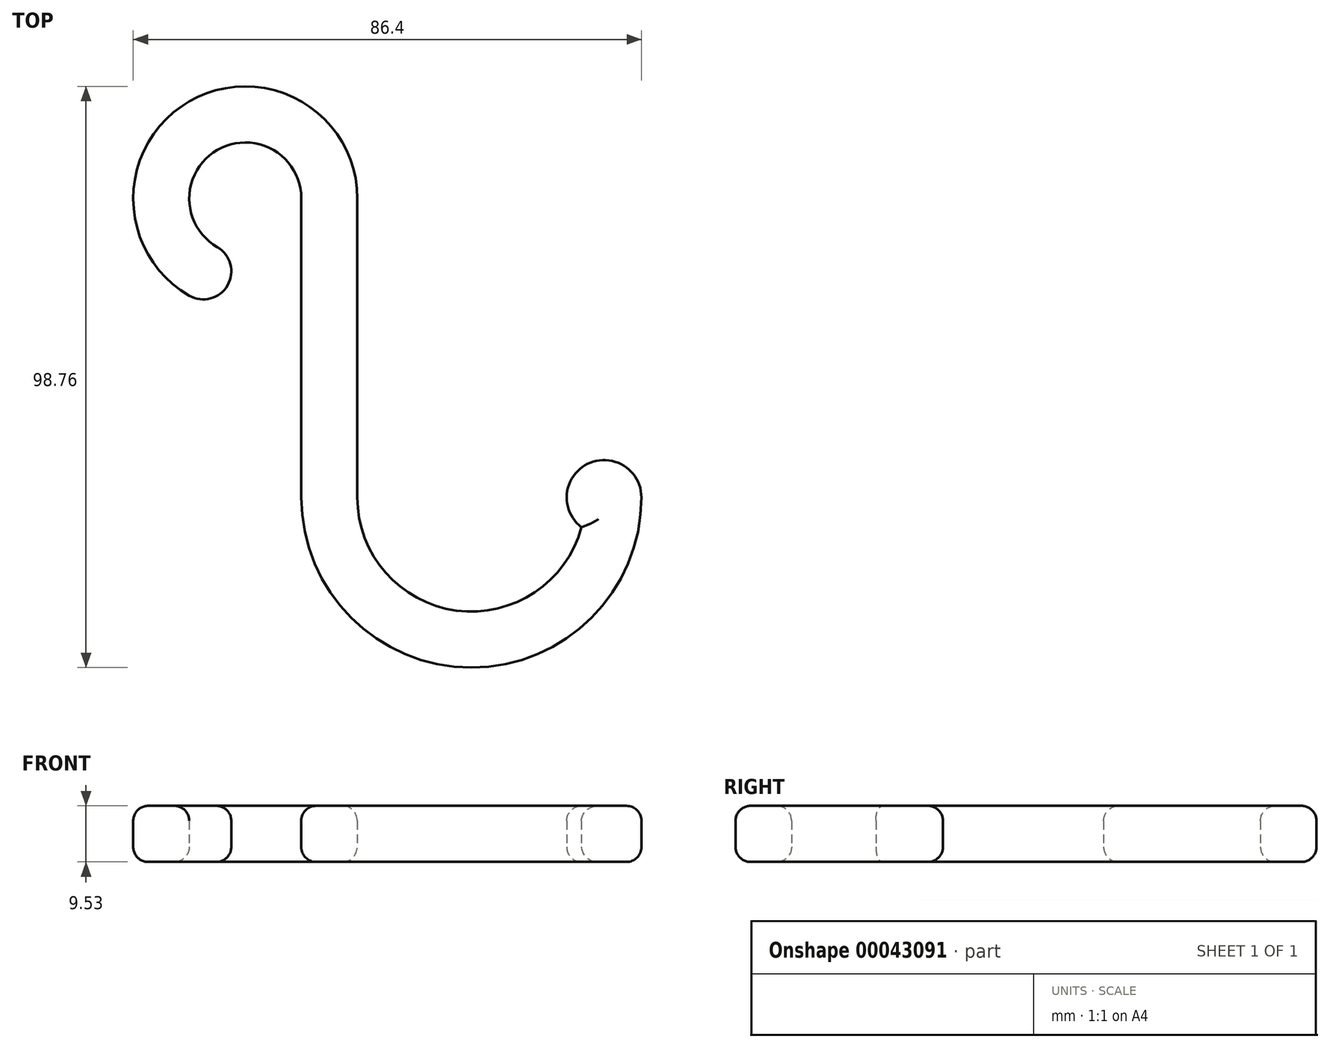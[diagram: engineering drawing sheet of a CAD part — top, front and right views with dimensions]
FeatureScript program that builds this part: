
annotation { "Feature Type Name" : "Feature", "Feature Type Description" : "" }
export const myFeature = defineFeature(function(context is Context, id is Id, definition is map)
    precondition{}
    {
        {
            var Q0;
            Q0=qCreatedBy(makeId("Top.planeOp"),FACE);
            var sketch = newSketch(context, id + "F0", { "sketchPlane" : qUnion([Q0])});
            skLineSegment(sketch, "E0.left", {"start": v(-9.52, 50.8) * mm, "end": v(-9.53, 0) * mm});
            skLineSegment(sketch, "E0.right", {"start": v(0, 50.8) * mm, "end": v(0, 0) * mm});
            skArc(sketch, "E1", {"start": v(0, 50.8) * mm, "mid": v(-28.57, 67.3) * mm, "end": v(-28.58, 34.3) * mm});
            skArc(sketch, "E2", {"start": v(-9.52, 50.8) * mm, "mid": v(-23.81, 59.05) * mm, "end": v(-23.81, 42.55) * mm});
            skArc(sketch, "E3", {"start": v(0, 0) * mm, "mid": v(16.84, -19.22) * mm, "end": v(38.1, -5.05) * mm});
            skArc(sketch, "E4", {"start": v(48.3, 0) * mm, "mid": v(19.39, -28.91) * mm, "end": v(-9.53, 0) * mm});
            skLineSegment(sketch, "E5", {"start": v(-19.05, 50.8) * mm, "end": v(-28.58, 34.3) * mm, "construction": true});
            skArc(sketch, "E6", {"start": v(-23.81, 42.55) * mm, "mid": v(-22.07, 36.05) * mm, "end": v(-28.58, 34.3) * mm});
            skArc(sketch, "E7", {"start": v(48.3, 0) * mm, "mid": v(39.13, 5.69) * mm, "end": v(38.1, -5.05) * mm});
            skLineSegment(sketch, "E8", {"start": v(38.16, -5.1) * mm, "end": v(38.1, -5.05) * mm, "construction": true});
            skLineSegment(sketch, "E9", {"start": v(38.1, -5.05) * mm, "end": v(34.63, -17.9) * mm, "construction": true});
            skSolve(sketch);
        }
        {
            var Q0;
            Q0 = qSketchRegion(id + "F0", true);
            extrude(context, id + "F1", {"entities" : qUnion([Q0]), "depth" : 9.52 * mm});
        }
        {
            var Q0;
            Q0=makeQuery(id+"F1.opExtrude","CAP_FACE",FACE,{"disambiguationData":[OSD([sQuery(id+"F0.wireOp",EDGE,"E0.left"),sQuery(id+"F0.wireOp",EDGE,"E0.right"),sQuery(id+"F0.wireOp",EDGE,"E1"),sQuery(id+"F0.wireOp",EDGE,"E2"),sQuery(id+"F0.wireOp",EDGE,"E3"),sQuery(id+"F0.wireOp",EDGE,"E4"),sQuery(id+"F0.wireOp",EDGE,"E6"),sQuery(id+"F0.wireOp",EDGE,"E7")])],"isStart":false});
            var Q1;
            Q1=makeQuery(id+"F1.opExtrude","CAP_FACE",FACE,{"disambiguationData":[OSD([sQuery(id+"F0.wireOp",EDGE,"E0.left"),sQuery(id+"F0.wireOp",EDGE,"E0.right"),sQuery(id+"F0.wireOp",EDGE,"E1"),sQuery(id+"F0.wireOp",EDGE,"E2"),sQuery(id+"F0.wireOp",EDGE,"E3"),sQuery(id+"F0.wireOp",EDGE,"E4"),sQuery(id+"F0.wireOp",EDGE,"E6"),sQuery(id+"F0.wireOp",EDGE,"E7")])],"isStart":true});
            fillet(context, id + "F2", {"entities" : qUnion([Q0, Q1]), "radius" : 2.54 * mm, "tangentPropagation" : true, "allowEdgeOverflow" : false});
        }
    });
